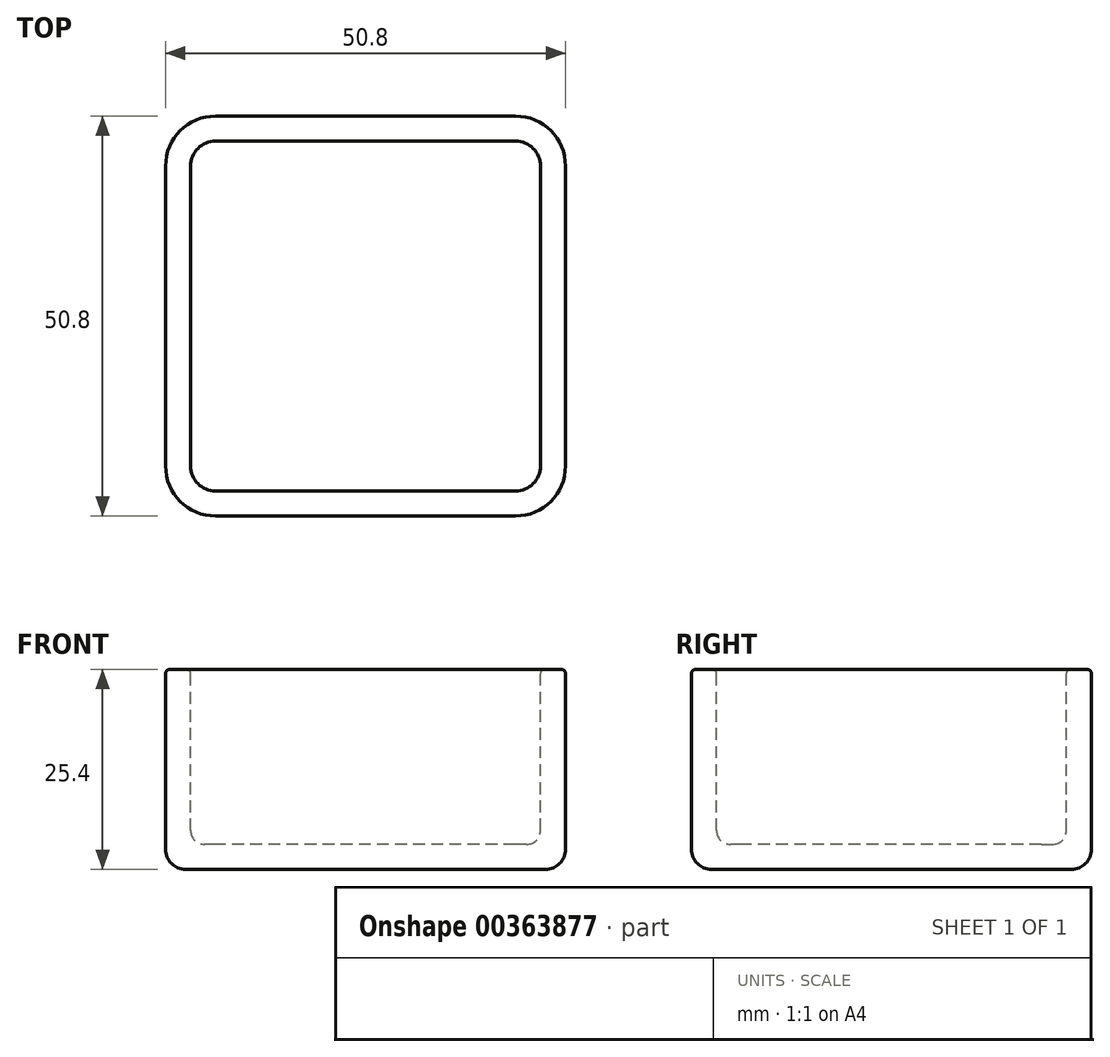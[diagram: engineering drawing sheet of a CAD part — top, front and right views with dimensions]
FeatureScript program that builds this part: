
annotation { "Feature Type Name" : "Feature", "Feature Type Description" : "" }
export const myFeature = defineFeature(function(context is Context, id is Id, definition is map)
    precondition{}
    {
        {
            var Q0;
            Q0=qCreatedBy(makeId("Top.planeOp"),FACE);
            var sketch = newSketch(context, id + "F0", { "sketchPlane" : qUnion([Q0])});
            skLineSegment(sketch, "E0.bottom", {"start": v(19.05, 28.6) * mm, "end": v(-19.05, 28.6) * mm});
            skLineSegment(sketch, "E0.top", {"start": v(19.05, -22.2) * mm, "end": v(-19.05, -22.2) * mm});
            skLineSegment(sketch, "E0.left", {"start": v(25.4, 22.26) * mm, "end": v(25.4, -15.84) * mm});
            skLineSegment(sketch, "E0.right", {"start": v(-25.4, 22.26) * mm, "end": v(-25.4, -15.84) * mm});
            skPoint(sketch, "E0.middle", {"position": v(0, 3.2) * mm});
            skPoint(sketch, "E1.visualSharp", {"position": v(-25.4, -22.2) * mm});
            skArc(sketch, "E1.filletArc", {"start": v(-25.4, -15.84) * mm, "mid": v(-23.54, -20.33) * mm, "end": v(-19.05, -22.2) * mm});
            skPoint(sketch, "E2.visualSharp", {"position": v(-25.4, 28.6) * mm});
            skArc(sketch, "E2.filletArc", {"start": v(-19.05, 28.6) * mm, "mid": v(-23.54, 26.75) * mm, "end": v(-25.4, 22.26) * mm});
            skPoint(sketch, "E3.visualSharp", {"position": v(25.4, 28.6) * mm});
            skArc(sketch, "E3.filletArc", {"start": v(25.4, 22.26) * mm, "mid": v(23.54, 26.75) * mm, "end": v(19.05, 28.6) * mm});
            skPoint(sketch, "E4.visualSharp", {"position": v(25.4, -22.2) * mm});
            skArc(sketch, "E4.filletArc", {"start": v(19.05, -22.2) * mm, "mid": v(23.54, -20.33) * mm, "end": v(25.4, -15.84) * mm});
            skSolve(sketch);
        }
        {
            var Q0;
            Q0 = qSketchRegion(id + "F0", true);
            extrude(context, id + "F1", {"entities" : qUnion([Q0]), "depth" : 25.4 * mm});
        }
        {
            var Q0;
            Q0=makeQuery(id+"F1.opExtrude","CAP_FACE",FACE,{"disambiguationData":[OSD([sQuery(id+"F0.wireOp",EDGE,"E0.bottom"),sQuery(id+"F0.wireOp",EDGE,"E0.top"),sQuery(id+"F0.wireOp",EDGE,"E0.left"),sQuery(id+"F0.wireOp",EDGE,"E0.right")])],"isStart":false});
            var sketch = newSketch(context, id + "F2", { "sketchPlane" : qUnion([Q0])});
            skArc(sketch, "E5.0", {"start": v(25.4, 22.26) * mm, "mid": v(23.54, 26.75) * mm, "end": v(19.05, 28.6) * mm});
            skLineSegment(sketch, "E5.1", {"start": v(25.4, 22.26) * mm, "end": v(25.4, -15.84) * mm});
            skArc(sketch, "E5.2", {"start": v(19.05, -22.2) * mm, "mid": v(23.54, -20.33) * mm, "end": v(25.4, -15.84) * mm});
            skLineSegment(sketch, "E5.3", {"start": v(19.05, -22.2) * mm, "end": v(-19.05, -22.2) * mm, "construction": true});
            skArc(sketch, "E5.4", {"start": v(-25.4, -15.84) * mm, "mid": v(-23.54, -20.33) * mm, "end": v(-19.05, -22.2) * mm});
            skLineSegment(sketch, "E5.5", {"start": v(-25.4, 22.26) * mm, "end": v(-25.4, -15.84) * mm});
            skArc(sketch, "E5.6", {"start": v(-19.05, 28.6) * mm, "mid": v(-23.54, 26.75) * mm, "end": v(-25.4, 22.26) * mm});
            skLineSegment(sketch, "E5.7", {"start": v(19.05, 28.6) * mm, "end": v(-19.05, 28.6) * mm});
            skArc(sketch, "E6.0", {"start": v(-19.05, 25.43) * mm, "mid": v(-21.3, 24.5) * mm, "end": v(-22.23, 22.26) * mm});
            skLineSegment(sketch, "E6.1", {"start": v(19.05, 25.43) * mm, "end": v(-19.05, 25.43) * mm});
            skLineSegment(sketch, "E6.2", {"start": v(-22.23, 22.26) * mm, "end": v(-22.23, -15.84) * mm});
            skArc(sketch, "E6.3", {"start": v(22.22, 22.26) * mm, "mid": v(21.3, 24.5) * mm, "end": v(19.05, 25.43) * mm});
            skArc(sketch, "E6.4", {"start": v(-22.23, -15.84) * mm, "mid": v(-21.3, -18.09) * mm, "end": v(-19.05, -19.02) * mm});
            skLineSegment(sketch, "E6.5", {"start": v(19.05, -19.02) * mm, "end": v(-19.05, -19.02) * mm});
            skArc(sketch, "E6.6", {"start": v(19.05, -19.02) * mm, "mid": v(21.3, -18.09) * mm, "end": v(22.22, -15.84) * mm});
            skLineSegment(sketch, "E6.7", {"start": v(22.22, 22.26) * mm, "end": v(22.22, -15.84) * mm});
            skSolve(sketch);
        }
        {
            var Q0;
            Q0 = qSketchRegion(id + "F2", true);
            extrude(context, id + "F3", {"entities" : qUnion([Q0]), "operationType" : NewBodyOperationType.REMOVE, "oppositeDirection" : true, "depth" : 22.22 * mm});
        }
        {
            var Q0;
            Q0=makeQuery(id+"F1.opExtrude","CAP_FACE",FACE,{"disambiguationData":[OSD([sQuery(id+"F0.wireOp",EDGE,"E0.bottom"),sQuery(id+"F0.wireOp",EDGE,"E0.top"),sQuery(id+"F0.wireOp",EDGE,"E0.left"),sQuery(id+"F0.wireOp",EDGE,"E0.right")])],"isStart":true});
            fillet(context, id + "F4", {"entities" : qUnion([Q0]), "radius" : 2.54 * mm, "tangentPropagation" : true, "allowEdgeOverflow" : false});
        }
        {
            var Q0;
            Q0=makeQuery(id+"F3.boolean.opBoolean","COPY",FACE,{"derivedFrom":makeQuery(id+"F3.opExtrude","CAP_FACE",FACE,{"disambiguationData":[OSD([sQuery(id+"F2.wireOp",EDGE,"E6.0"),sQuery(id+"F2.wireOp",EDGE,"E6.1"),sQuery(id+"F2.wireOp",EDGE,"E6.2"),sQuery(id+"F2.wireOp",EDGE,"E6.3"),sQuery(id+"F2.wireOp",EDGE,"E6.4"),sQuery(id+"F2.wireOp",EDGE,"E6.5"),sQuery(id+"F2.wireOp",EDGE,"E6.6"),sQuery(id+"F2.wireOp",EDGE,"E6.7")])],"isStart":false})});
            fillet(context, id + "F5", {"entities" : qUnion([Q0]), "radius" : 1.78 * mm, "tangentPropagation" : true, "allowEdgeOverflow" : false});
        }
        {
            var Q0;
            Q0=makeQuery(id+"F1.opExtrude","CAP_FACE",FACE,{"disambiguationData":[OSD([sQuery(id+"F0.wireOp",EDGE,"E0.bottom"),sQuery(id+"F0.wireOp",EDGE,"E0.top"),sQuery(id+"F0.wireOp",EDGE,"E0.left"),sQuery(id+"F0.wireOp",EDGE,"E0.right")])],"isStart":false});
            fillet(context, id + "F6", {"entities" : qUnion([Q0]), "radius" : 0.5 * mm, "tangentPropagation" : true, "allowEdgeOverflow" : false});
        }
    });
